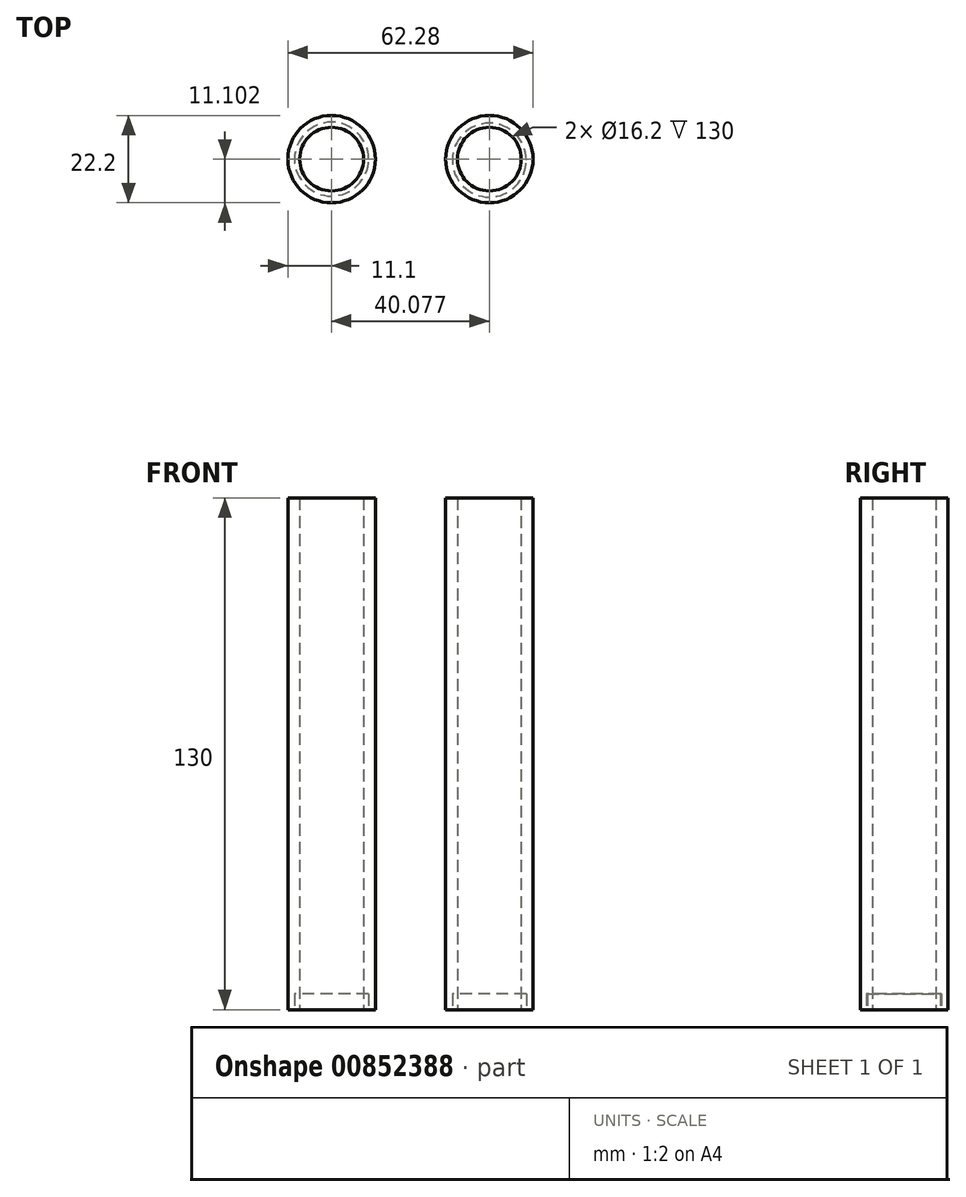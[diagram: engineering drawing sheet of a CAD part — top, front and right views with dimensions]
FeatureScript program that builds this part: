
annotation { "Feature Type Name" : "Feature", "Feature Type Description" : "" }
export const myFeature = defineFeature(function(context is Context, id is Id, definition is map)
    precondition{}
    {
        {
            var Q0;
            Q0=qCreatedBy(makeId("Top.planeOp"),FACE);
            var sketch = newSketch(context, id + "F0", { "sketchPlane" : qUnion([Q0])});
            skCircle(sketch, "E0", {"center": v(-21.57, 11.23) * mm, "radius": 8.1 * mm});
            skCircle(sketch, "E1", {"center": v(-21.57, 11.23) * mm, "radius": 11.1 * mm});
            skCircle(sketch, "E2", {"center": v(18.5, 11.23) * mm, "radius": 8.1 * mm});
            skCircle(sketch, "E3", {"center": v(18.5, 11.23) * mm, "radius": 11.1 * mm});
            skSolve(sketch);
        }
        {
            var Q0;
            Q0=makeQuery(id+"F0.imprint","IMPRINT",FACE,{"disambiguationData":[TD([[makeQuery(id+"F0.imprint","IMPRINT",EDGE,{"derivedFrom":sQuery(id+"F0.wireOp",EDGE,"E0")}),-1.0]])]});
            extrude(context, id + "F1", {"entities" : qUnion([Q0]), "depth" : 130 * mm, "offsetDistance" : 25 * mm});
        }
        {
            var Q0;
            Q0 = qSketchRegion(id + "F0", true);
            extrude(context, id + "F2", {"entities" : qUnion([Q0]), "operationType" : NewBodyOperationType.ADD, "depth" : 130 * mm, "offsetDistance" : 25 * mm});
        }
        {
            var Q0;
            Q0=qCreatedBy(makeId("Top.planeOp"),FACE);
            var sketch = newSketch(context, id + "F3", { "sketchPlane" : qUnion([Q0])});
            skCircle(sketch, "E4", {"center": v(-21.57, 11.23) * mm, "radius": 9.4 * mm});
            skCircle(sketch, "E5", {"center": v(18.5, 10.98) * mm, "radius": 9.4 * mm});
            skSolve(sketch);
        }
        {
            var Q0;
            Q0=makeQuery(id+"F3.imprint","IMPRINT",FACE,{"disambiguationData":[TD([[makeQuery(id+"F3.imprint","IMPRINT",EDGE,{"derivedFrom":sQuery(id+"F3.wireOp",EDGE,"E5")}),1.0]])]});
            var Q1;
            Q1=makeQuery(id+"F3.imprint","IMPRINT",FACE,{"disambiguationData":[TD([[makeQuery(id+"F3.imprint","IMPRINT",EDGE,{"derivedFrom":sQuery(id+"F3.wireOp",EDGE,"E4")}),1.0]])]});
            extrude(context, id + "F4", {"entities" : qUnion([Q0, Q1]), "depth" : 4 * mm, "offsetDistance" : 25 * mm});
        }
    });
